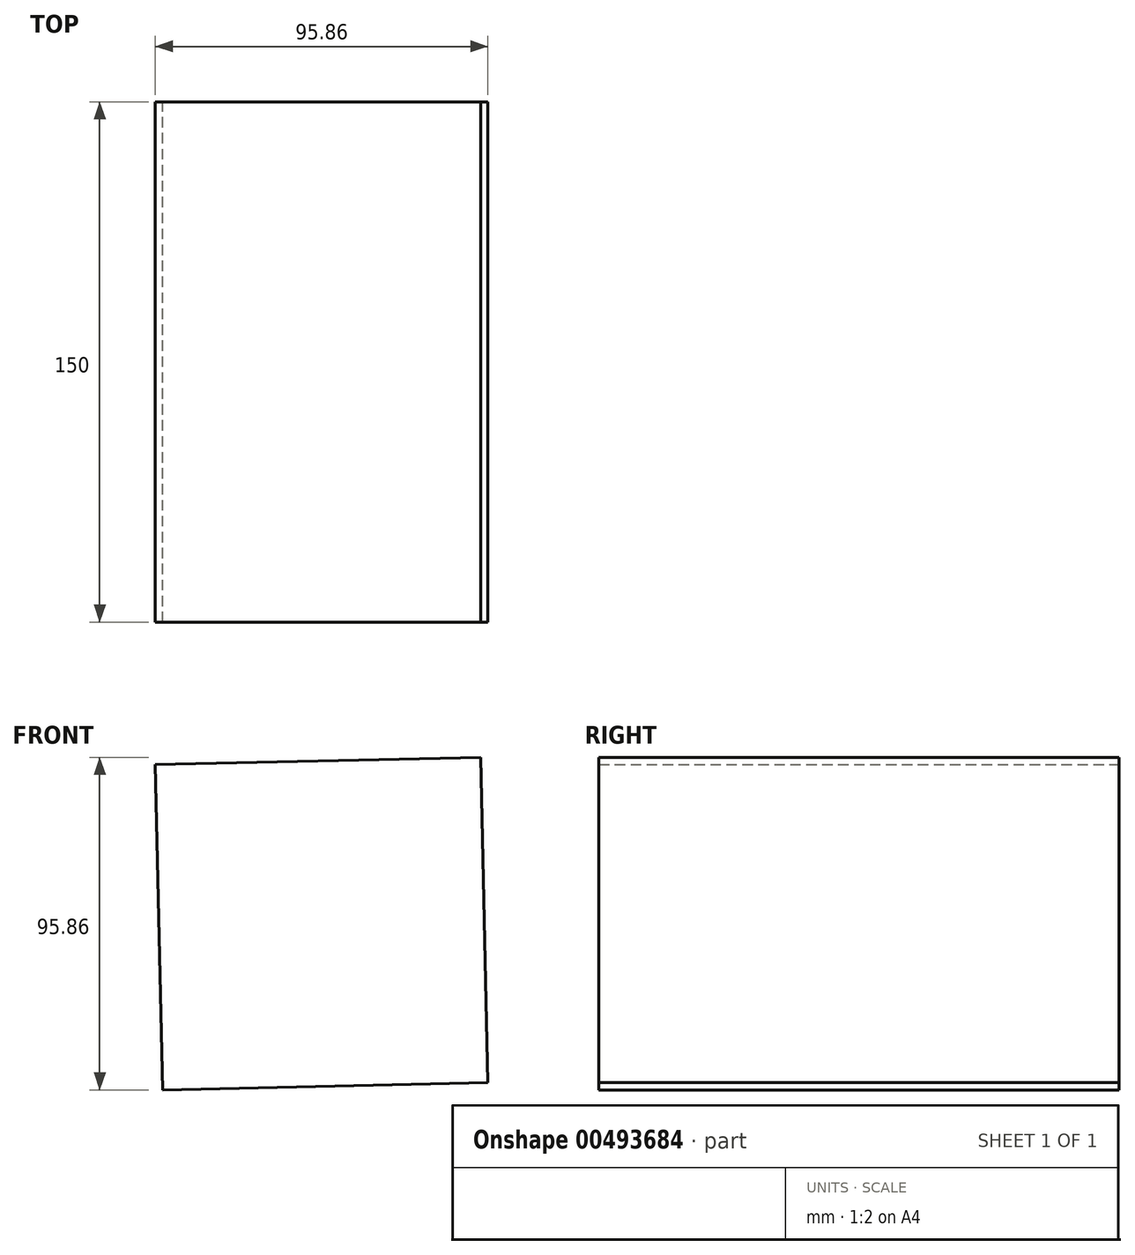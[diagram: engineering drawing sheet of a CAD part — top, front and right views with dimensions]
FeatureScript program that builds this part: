
annotation { "Feature Type Name" : "Feature", "Feature Type Description" : "" }
export const myFeature = defineFeature(function(context is Context, id is Id, definition is map)
    precondition{}
    {
        {
            var Q0;
            Q0=qCreatedBy(makeId("Front.planeOp"),FACE);
            var sketch = newSketch(context, id + "F0", { "sketchPlane" : qUnion([Q0])});
            skCircle(sketch, "E0.cCircle", {"center": v(0, 0) * mm, "radius": 66.31 * mm, "construction": true});
            skLineSegment(sketch, "E0.0", {"start": v(-45.83, -47.93) * mm, "end": v(-47.93, 45.83) * mm});
            skLineSegment(sketch, "E0.1", {"start": v(-47.93, 45.83) * mm, "end": v(45.83, 47.93) * mm});
            skLineSegment(sketch, "E0.2", {"start": v(45.83, 47.93) * mm, "end": v(47.93, -45.83) * mm});
            skLineSegment(sketch, "E0.3", {"start": v(47.93, -45.83) * mm, "end": v(-45.83, -47.93) * mm});
            skSolve(sketch);
        }
        {
            var Q0;
            Q0=makeQuery(id+"F0.imprint","IMPRINT",FACE,{"disambiguationData":[TD([[makeQuery(id+"F0.imprint","IMPRINT",EDGE,{"derivedFrom":sQuery(id+"F0.wireOp",EDGE,"E0.0")}),-1.0]])]});
            extrude(context, id + "F1", {"entities" : qUnion([Q0]), "depth" : 150 * mm});
        }
    });
